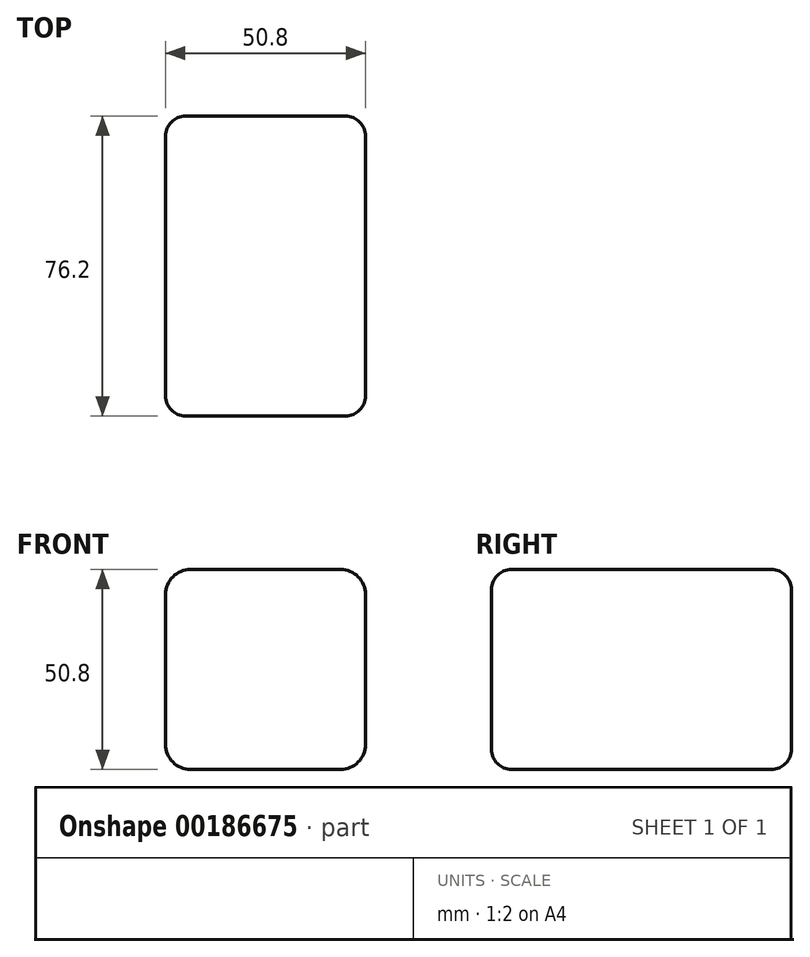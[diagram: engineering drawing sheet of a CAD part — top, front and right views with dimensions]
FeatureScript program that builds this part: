
annotation { "Feature Type Name" : "Feature", "Feature Type Description" : "" }
export const myFeature = defineFeature(function(context is Context, id is Id, definition is map)
    precondition{}
    {
        {
            var Q0;
            Q0=qCreatedBy(makeId("Front.planeOp"),FACE);
            var sketch = newSketch(context, id + "F0", { "sketchPlane" : qUnion([Q0])});
            skLineSegment(sketch, "E0", {"start": v(-26.54, 14.2) * mm, "end": v(-26.54, -23.9) * mm});
            skLineSegment(sketch, "E1", {"start": v(-20.2, -30.24) * mm, "end": v(17.9, -30.24) * mm});
            skLineSegment(sketch, "E2", {"start": v(24.26, -23.9) * mm, "end": v(24.26, 14.2) * mm});
            skLineSegment(sketch, "E3", {"start": v(17.9, 20.56) * mm, "end": v(-20.2, 20.56) * mm});
            skPoint(sketch, "E4.visualSharp", {"position": v(24.26, 20.56) * mm});
            skArc(sketch, "E4.filletArc", {"start": v(24.26, 14.2) * mm, "mid": v(22.4, 18.7) * mm, "end": v(17.9, 20.56) * mm});
            skPoint(sketch, "E5.visualSharp", {"position": v(-26.54, 20.56) * mm});
            skArc(sketch, "E5.filletArc", {"start": v(-20.2, 20.56) * mm, "mid": v(-24.68, 18.7) * mm, "end": v(-26.54, 14.2) * mm});
            skPoint(sketch, "E6.visualSharp", {"position": v(-26.54, -30.24) * mm});
            skArc(sketch, "E6.filletArc", {"start": v(-26.54, -23.9) * mm, "mid": v(-24.68, -28.38) * mm, "end": v(-20.2, -30.24) * mm});
            skPoint(sketch, "E7.visualSharp", {"position": v(24.26, -30.24) * mm});
            skArc(sketch, "E7.filletArc", {"start": v(17.9, -30.24) * mm, "mid": v(22.4, -28.38) * mm, "end": v(24.26, -23.9) * mm});
            skSolve(sketch);
        }
        {
            var Q0;
            Q0=makeQuery(id+"F0.imprint","IMPRINT",FACE,{"disambiguationData":[TD([[makeQuery(id+"F0.imprint","IMPRINT",EDGE,{"derivedFrom":sQuery(id+"F0.wireOp",EDGE,"E0")}),1.0]])]});
            extrude(context, id + "F1", {"entities" : qUnion([Q0]), "depth" : 25.4 * mm});
        }
        {
            var Q0;
            Q0=makeQuery(id+"F1.opExtrude","CAP_FACE",FACE,{"disambiguationData":[OSD([sQuery(id+"F0.wireOp",EDGE,"E0"),sQuery(id+"F0.wireOp",EDGE,"E1"),sQuery(id+"F0.wireOp",EDGE,"E2"),sQuery(id+"F0.wireOp",EDGE,"E3"),sQuery(id+"F0.wireOp",EDGE,"E4.filletArc"),sQuery(id+"F0.wireOp",EDGE,"E5.filletArc"),sQuery(id+"F0.wireOp",EDGE,"E6.filletArc"),sQuery(id+"F0.wireOp",EDGE,"E7.filletArc")])],"isStart":false});
            extrude(context, id + "F2", {"entities" : qUnion([Q0]), "operationType" : NewBodyOperationType.ADD, "depth" : 50.8 * mm});
        }
        {
            var Q0;
            Q0=makeQuery(id+"F2.opExtrude","CAP_EDGE",EDGE,{"disambiguationData":[OSD([sQuery(id+"F0.wireOp",EDGE,"E0")])],"isStart":false});
            fillet(context, id + "F3", {"entities" : qUnion([Q0]), "radius" : 5.08 * mm, "tangentPropagation" : true, "allowEdgeOverflow" : false});
        }
        {
            var Q0;
            Q0=makeQuery(id+"F1.opExtrude","CAP_FACE",FACE,{"disambiguationData":[OSD([sQuery(id+"F0.wireOp",EDGE,"E0"),sQuery(id+"F0.wireOp",EDGE,"E1"),sQuery(id+"F0.wireOp",EDGE,"E2"),sQuery(id+"F0.wireOp",EDGE,"E3"),sQuery(id+"F0.wireOp",EDGE,"E4.filletArc"),sQuery(id+"F0.wireOp",EDGE,"E5.filletArc"),sQuery(id+"F0.wireOp",EDGE,"E6.filletArc"),sQuery(id+"F0.wireOp",EDGE,"E7.filletArc")])],"isStart":true});
            fillet(context, id + "F4", {"entities" : qUnion([Q0]), "radius" : 5.08 * mm, "tangentPropagation" : true, "allowEdgeOverflow" : false});
        }
    });
